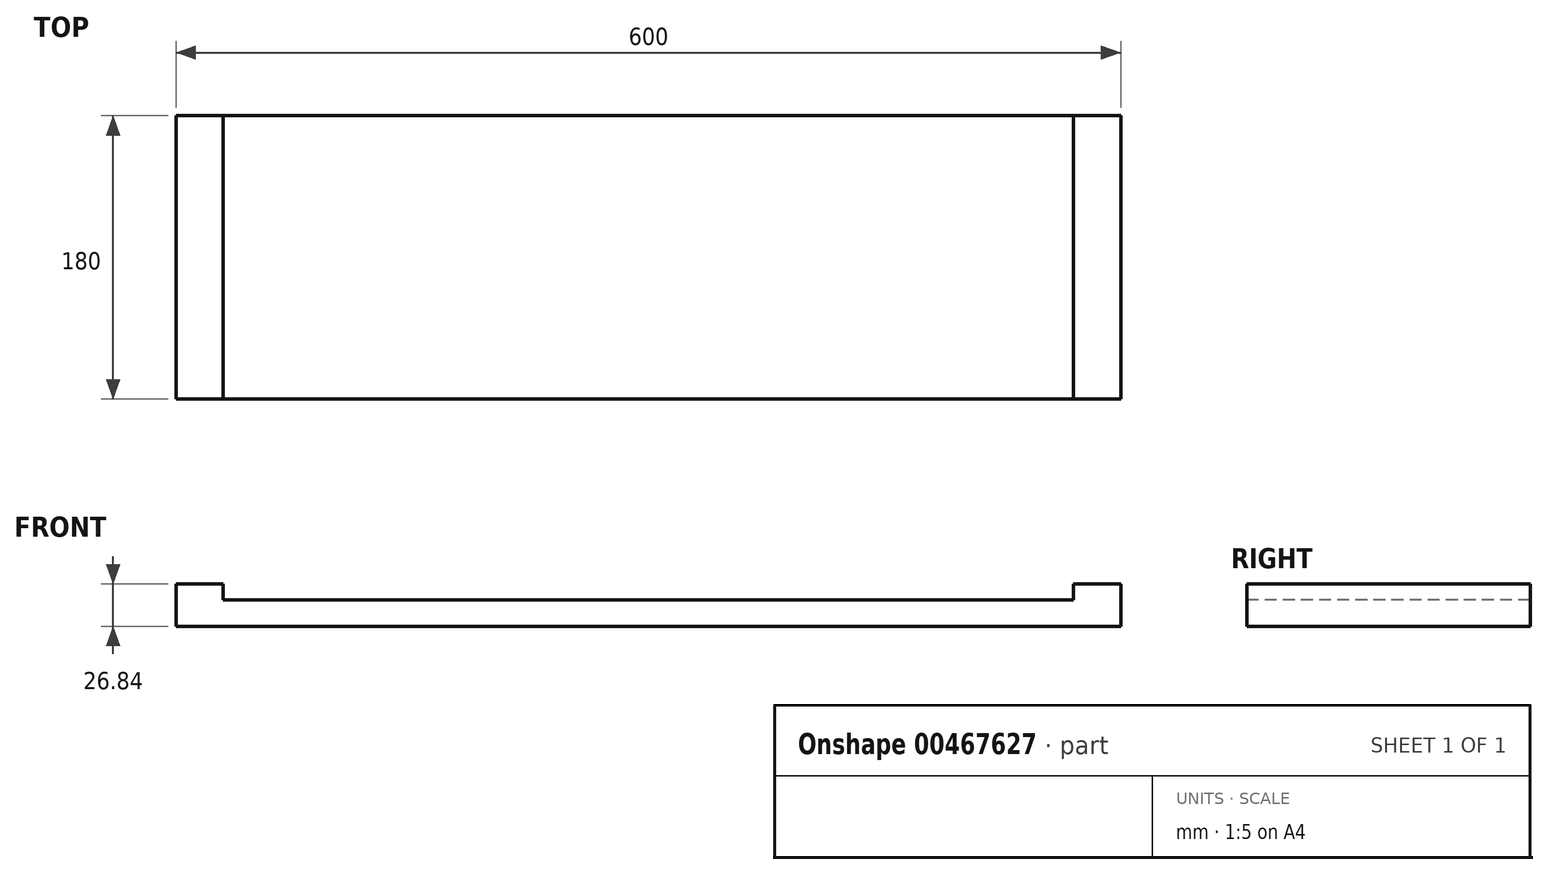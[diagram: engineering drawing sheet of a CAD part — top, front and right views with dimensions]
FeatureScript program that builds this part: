
annotation { "Feature Type Name" : "Feature", "Feature Type Description" : "" }
export const myFeature = defineFeature(function(context is Context, id is Id, definition is map)
    precondition{}
    {
        {
            var Q0;
            Q0=qCreatedBy(makeId("Top.planeOp"),FACE);
            var sketch = newSketch(context, id + "F0", { "sketchPlane" : qUnion([Q0])});
            skLineSegment(sketch, "E0.bottom", {"start": v(0, 0) * mm, "end": v(600, 0) * mm});
            skLineSegment(sketch, "E0.top", {"start": v(0, -180) * mm, "end": v(600, -180) * mm});
            skLineSegment(sketch, "E0.left", {"start": v(0, 0) * mm, "end": v(0, -180) * mm});
            skLineSegment(sketch, "E0.right", {"start": v(600, 0) * mm, "end": v(600, -180) * mm});
            skSolve(sketch);
        }
        {
            var Q0;
            Q0 = qSketchRegion(id + "F0", true);
            extrude(context, id + "F1", {"entities" : qUnion([Q0]), "depth" : 16.84 * mm});
        }
        {
            var Q0;
            Q0=makeQuery(id+"F1.opExtrude","CAP_FACE",FACE,{"disambiguationData":[OSD([sQuery(id+"F0.wireOp",EDGE,"E0.bottom"),sQuery(id+"F0.wireOp",EDGE,"E0.top"),sQuery(id+"F0.wireOp",EDGE,"E0.left"),sQuery(id+"F0.wireOp",EDGE,"E0.right")])],"isStart":false});
            var sketch = newSketch(context, id + "F2", { "sketchPlane" : qUnion([Q0])});
            skLineSegment(sketch, "E1.bottom", {"start": v(600, -180) * mm, "end": v(570, -180) * mm});
            skLineSegment(sketch, "E1.top", {"start": v(600, 0) * mm, "end": v(570, 0) * mm});
            skLineSegment(sketch, "E1.left", {"start": v(600, -180) * mm, "end": v(600, 0) * mm});
            skLineSegment(sketch, "E1.right", {"start": v(570, -180) * mm, "end": v(570, 0) * mm});
            skSolve(sketch);
        }
        {
            var Q0;
            Q0 = qSketchRegion(id + "F2", true);
            extrude(context, id + "F3", {"entities" : qUnion([Q0]), "operationType" : NewBodyOperationType.ADD, "depth" : 10 * mm});
        }
        {
            var Q0;
            Q0=makeQuery(id+"F1.opExtrude","CAP_FACE",FACE,{"disambiguationData":[OSD([sQuery(id+"F0.wireOp",EDGE,"E0.bottom"),sQuery(id+"F0.wireOp",EDGE,"E0.top"),sQuery(id+"F0.wireOp",EDGE,"E0.left"),sQuery(id+"F0.wireOp",EDGE,"E0.right")])],"isStart":false});
            var sketch = newSketch(context, id + "F4", { "sketchPlane" : qUnion([Q0])});
            skLineSegment(sketch, "E2.bottom", {"start": v(0, 0) * mm, "end": v(30, 0) * mm});
            skLineSegment(sketch, "E2.top", {"start": v(0, -180) * mm, "end": v(30, -180) * mm, "construction": true});
            skLineSegment(sketch, "E2.left", {"start": v(0, 0) * mm, "end": v(0, -180) * mm});
            skLineSegment(sketch, "E2.right", {"start": v(30, 0) * mm, "end": v(30, -180) * mm});
            skSolve(sketch);
        }
        {
            var Q0;
            Q0=makeQuery(id+"F4.imprint","IMPRINT",FACE,{"disambiguationData":[TD([[makeQuery(id+"F4.imprint","IMPRINT",EDGE,{"derivedFrom":sQuery(id+"F4.wireOp",EDGE,"E2.bottom")}),-1.0]])]});
            extrude(context, id + "F5", {"entities" : qUnion([Q0]), "operationType" : NewBodyOperationType.ADD, "depth" : 10 * mm});
        }
    });
